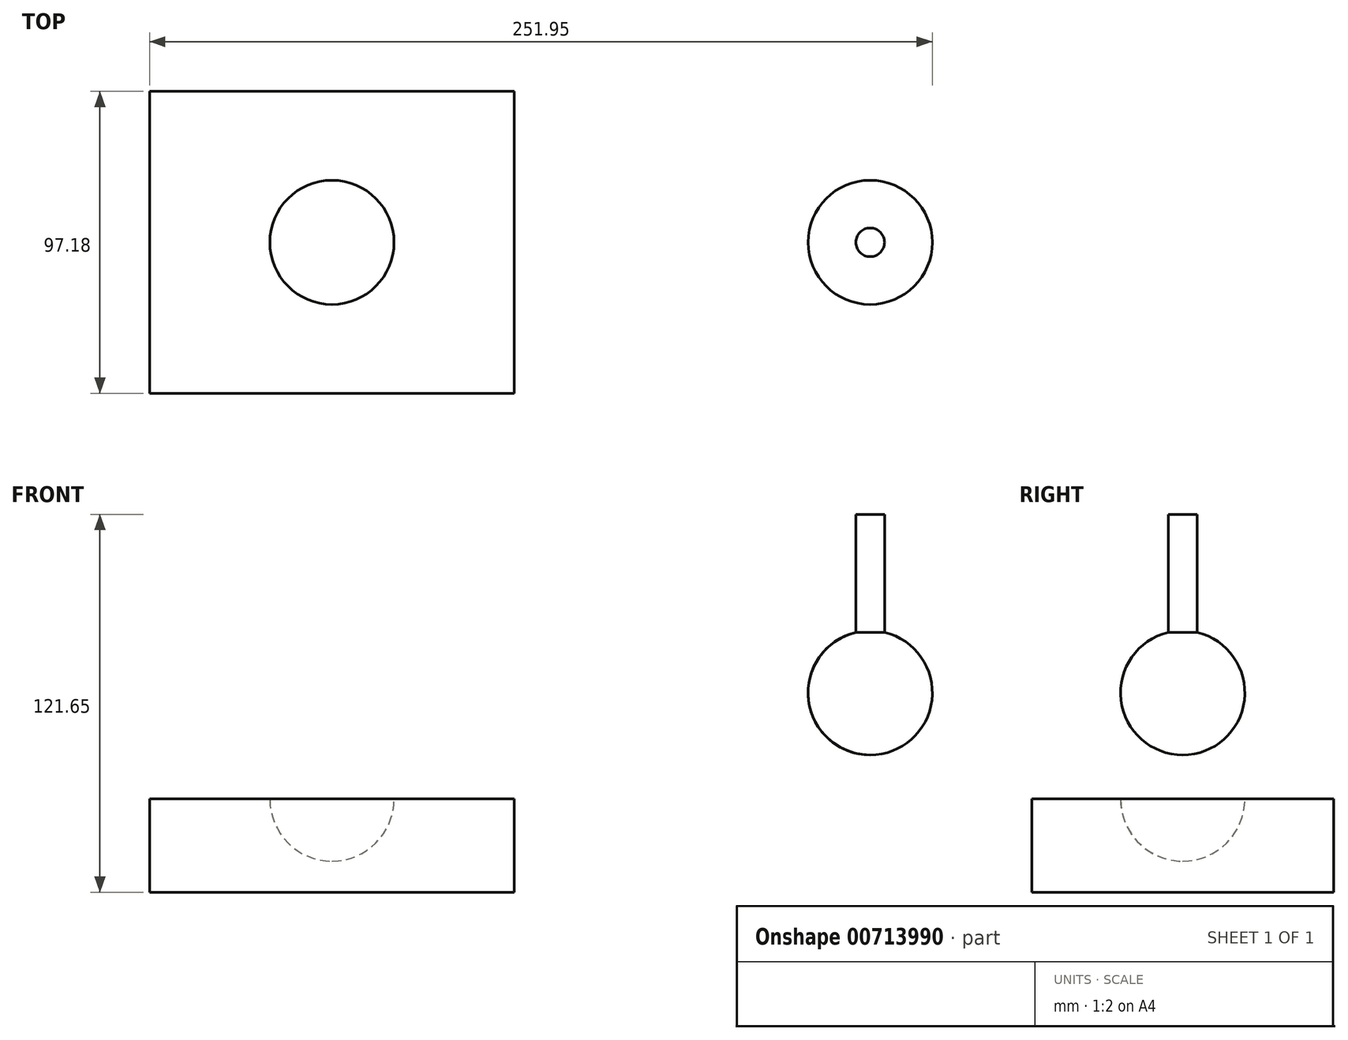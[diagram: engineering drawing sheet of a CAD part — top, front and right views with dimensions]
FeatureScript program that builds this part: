
annotation { "Feature Type Name" : "Feature", "Feature Type Description" : "" }
export const myFeature = defineFeature(function(context is Context, id is Id, definition is map)
    precondition{}
    {
        {
            var Q0;
            Q0=qCreatedBy(makeId("Top.planeOp"),FACE);
            var sketch = newSketch(context, id + "F0", { "sketchPlane" : qUnion([Q0])});
            skLineSegment(sketch, "E0.rect.bottom", {"start": v(-58.68, 48.6) * mm, "end": v(58.68, 48.6) * mm});
            skLineSegment(sketch, "E0.rect.top", {"start": v(-58.68, -48.6) * mm, "end": v(58.68, -48.6) * mm});
            skLineSegment(sketch, "E0.rect.left", {"start": v(-58.68, 48.6) * mm, "end": v(-58.68, -48.6) * mm});
            skLineSegment(sketch, "E0.rect.right", {"start": v(58.68, 48.6) * mm, "end": v(58.68, -48.6) * mm});
            skPoint(sketch, "E0.rect.middle", {"position": v(0, 0) * mm});
            skSolve(sketch);
        }
        {
            var Q0;
            Q0=qSketchRegion(id+"F0",true);
            extrude(context, id + "F1", {"entities" : qUnion([Q0]), "oppositeDirection" : true, "depth" : 30 * mm});
        }
        {
            var Q0;
            Q0=qCreatedBy(makeId("Right.planeOp"),FACE);
            var sketch = newSketch(context, id + "F2", { "sketchPlane" : qUnion([Q0])});
            skArc(sketch, "E1", {"start": v(0, -20) * mm, "mid": v(20, 0) * mm, "end": v(0, 20) * mm});
            skLineSegment(sketch, "E2", {"start": v(0, 20) * mm, "end": v(0, -20) * mm});
            skSolve(sketch);
        }
        {
            var Q0;
            Q0=qSketchRegion(id+"F2",true);
            var Q1;
            Q1=sQuery(id+"F2.wireOp",EDGE,"E2");
            revolve(context, id + "F3", {"operationType" : NewBodyOperationType.REMOVE, "entities" : qUnion([Q0]), "axis" : qUnion([Q1]), "revolveType" : RevolveType.FULL, "oppositeDirection" : true});
        }
        {
            var Q0;
            Q0=qCreatedBy(makeId("Front.planeOp"),FACE);
            var sketch = newSketch(context, id + "F4", { "sketchPlane" : qUnion([Q0])});
            skArc(sketch, "E3", {"start": v(173.27, 14.2) * mm, "mid": v(193.13, 31.86) * mm, "end": v(177.9, 53.65) * mm});
            skLineSegment(sketch, "E4", {"start": v(173.27, 14.2) * mm, "end": v(173.27, 91.65) * mm});
            skLineSegment(sketch, "E5", {"start": v(173.27, 91.65) * mm, "end": v(177.9, 91.65) * mm});
            skLineSegment(sketch, "E6", {"start": v(177.9, 91.65) * mm, "end": v(177.9, 53.65) * mm});
            skSolve(sketch);
        }
        {
            var Q0;
            Q0=makeQuery(id+"F4.imprint","IMPRINT",FACE,{"disambiguationData":[TD([[makeQuery(id+"F4.imprint","IMPRINT",EDGE,{"derivedFrom":sQuery(id+"F4.wireOp",EDGE,"E3")}),1.0]])]});
            var Q1;
            Q1=sQuery(id+"F4.wireOp",EDGE,"E4");
            revolve(context, id + "F5", {"entities" : qUnion([Q0]), "axis" : qUnion([Q1]), "revolveType" : RevolveType.FULL});
        }
    });
